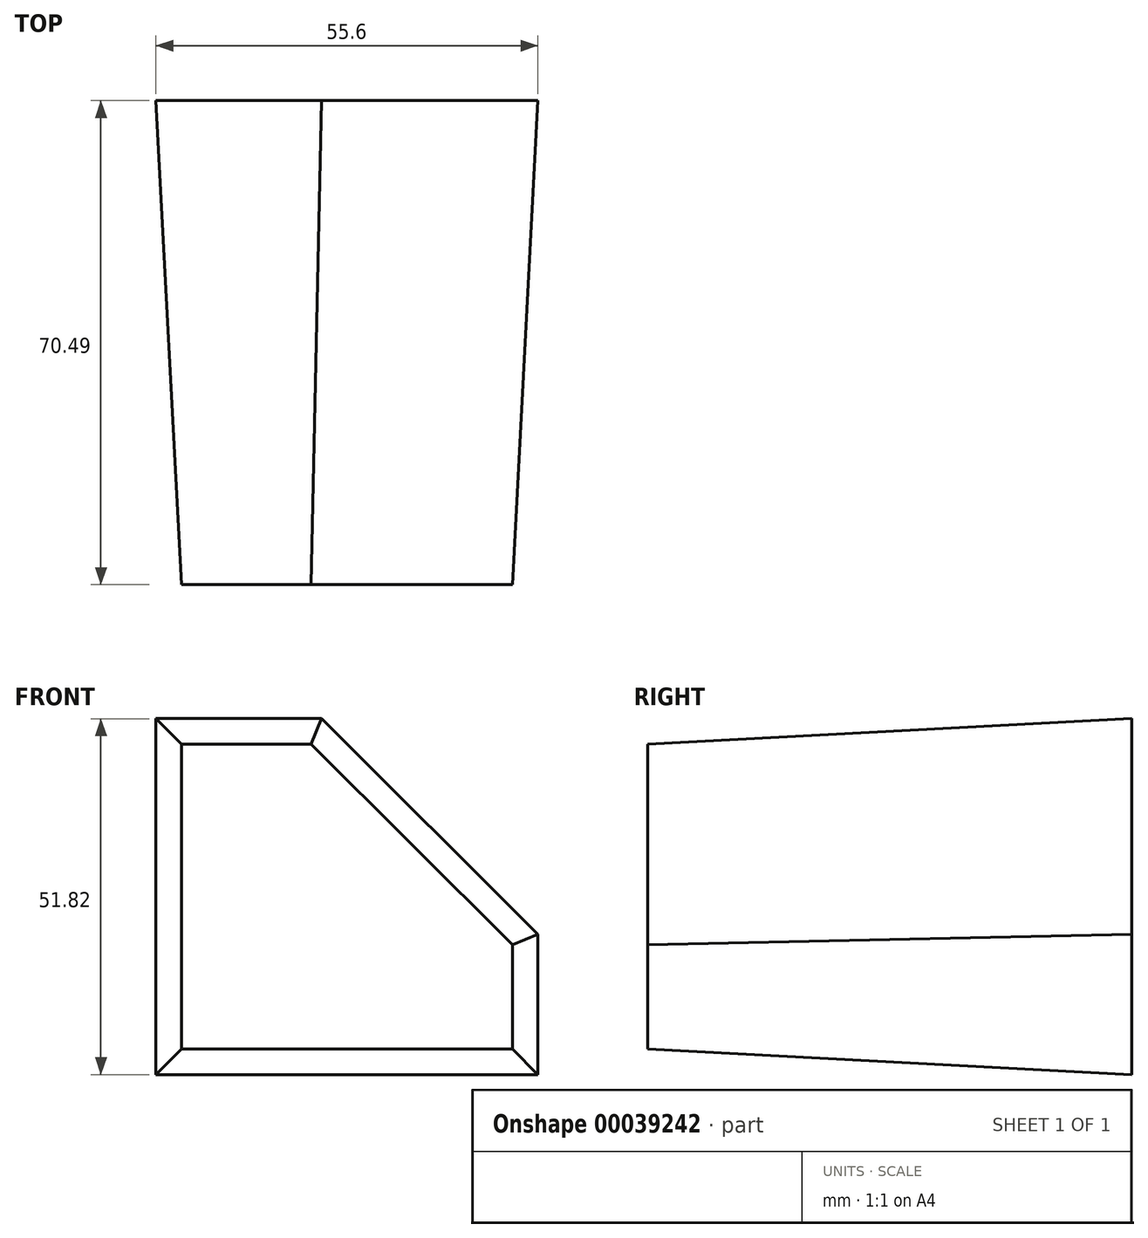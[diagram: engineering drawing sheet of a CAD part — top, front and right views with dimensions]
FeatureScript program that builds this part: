
annotation { "Feature Type Name" : "Feature", "Feature Type Description" : "" }
export const myFeature = defineFeature(function(context is Context, id is Id, definition is map)
    precondition{}
    {
        {
            var Q0;
            Q0=qCreatedBy(makeId("Front.planeOp"),FACE);
            var sketch = newSketch(context, id + "F0", { "sketchPlane" : qUnion([Q0])});
            skLineSegment(sketch, "E0", {"start": v(-105.24, 0) * mm, "end": v(-105.24, 51.82) * mm});
            skLineSegment(sketch, "E1", {"start": v(-105.24, 51.82) * mm, "end": v(-81.13, 51.82) * mm});
            skLineSegment(sketch, "E2", {"start": v(-81.13, 51.82) * mm, "end": v(-49.64, 20.42) * mm});
            skLineSegment(sketch, "E3", {"start": v(-49.64, 20.42) * mm, "end": v(-49.64, 0) * mm});
            skLineSegment(sketch, "E4", {"start": v(-49.64, 0) * mm, "end": v(-105.24, 0) * mm});
            skSolve(sketch);
        }
        {
            var Q0;
            Q0=makeQuery(id+"F0.imprint","IMPRINT",FACE,{"disambiguationData":[TD([[makeQuery(id+"F0.imprint","IMPRINT",EDGE,{"derivedFrom":sQuery(id+"F0.wireOp",EDGE,"E0")}),-1.0]])]});
            extrude(context, id + "F1", {"entities" : qUnion([Q0]), "depth" : 70.49 * mm, "hasDraft" : true, "draftAngle" : 3 * degree, "draftPullDirection" : true});
        }
    });
